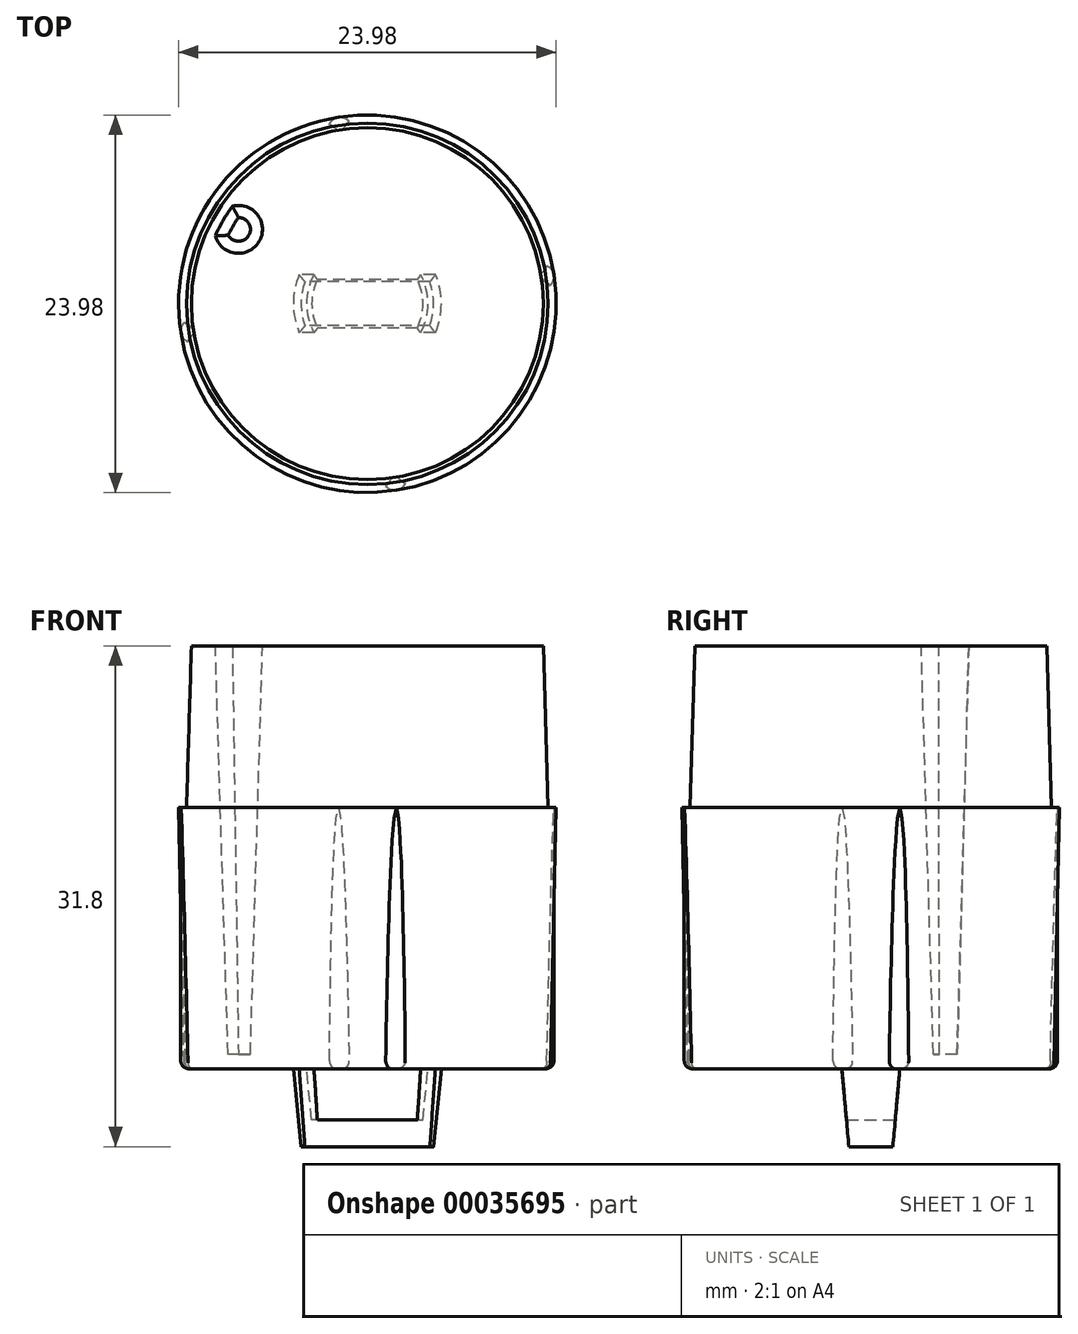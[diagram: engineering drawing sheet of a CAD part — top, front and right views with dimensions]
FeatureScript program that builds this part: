
annotation { "Feature Type Name" : "Feature", "Feature Type Description" : "" }
export const myFeature = defineFeature(function(context is Context, id is Id, definition is map)
    precondition{}
    {
        {
            var Q0;
            Q0=qCreatedBy(makeId("Front.planeOp"),FACE);
            var sketch = newSketch(context, id + "F0", { "sketchPlane" : qUnion([Q0])});
            skPoint(sketch, "E0.visualSharp", {"position": v(11.63, 0) * mm});
            skLineSegment(sketch, "E1", {"start": v(0, 0) * mm, "end": v(11.26, 0) * mm});
            skLineSegment(sketch, "E2", {"start": v(11.64, 0.37) * mm, "end": v(11.99, 16.59) * mm});
            skLineSegment(sketch, "E3", {"start": v(11.32, 16.59) * mm, "end": v(11.18, 26.85) * mm});
            skLineSegment(sketch, "E4", {"start": v(10.58, 26.85) * mm, "end": v(9.86, 0.91) * mm});
            skLineSegment(sketch, "E5", {"start": v(9.86, 0.91) * mm, "end": v(0, 0.91) * mm});
            skLineSegment(sketch, "E6", {"start": v(0, -4.95) * mm, "end": v(4.2, -4.95) * mm});
            skLineSegment(sketch, "E7", {"start": v(4.2, -4.95) * mm, "end": v(4.7, 0) * mm});
            skLineSegment(sketch, "E8", {"start": v(3.53, -3.25) * mm, "end": v(3.95, 0.91) * mm});
            skLineSegment(sketch, "E9", {"start": v(0, -3.25) * mm, "end": v(0, -4.95) * mm});
            skLineSegment(sketch, "E10", {"start": v(11.99, 16.59) * mm, "end": v(11.32, 16.59) * mm});
            skLineSegment(sketch, "E11", {"start": v(11.18, 26.85) * mm, "end": v(10.58, 26.85) * mm});
            skLineSegment(sketch, "E12", {"start": v(0, 0.91) * mm, "end": v(0, 0) * mm});
            skLineSegment(sketch, "E13", {"start": v(0, -3.25) * mm, "end": v(3.53, -3.25) * mm});
            skArc(sketch, "E0.filletArc", {"start": v(11.26, 0) * mm, "mid": v(11.53, 0.1) * mm, "end": v(11.64, 0.37) * mm});
            skSolve(sketch);
        }
        {
            var Q0;
            Q0=makeQuery(id+"F0.imprint","IMPRINT",FACE,{"disambiguationData":[TD([[makeQuery(id+"F0.imprint","IMPRINT",EDGE,{"derivedFrom":sQuery(id+"F0.wireOp",EDGE,"E2")}),1.0]])]});
            var Q1;
            Q1=makeQuery(id+"F0.imprint","IMPRINT",FACE,{"disambiguationData":[TD([[makeQuery(id+"F0.imprint","IMPRINT",EDGE,{"derivedFrom":sQuery(id+"F0.wireOp",EDGE,"E6")}),1.0]])]});
            var Q2;
            Q2=sQuery(id+"F0.wireOp",EDGE,"E12");
            revolve(context, id + "F1", {"entities" : qUnion([Q0, Q1]), "axis" : qUnion([Q2]), "revolveType" : RevolveType.FULL});
        }
        {
            var Q0;
            Q0=qCreatedBy(makeId("Right.planeOp"),FACE);
            var sketch = newSketch(context, id + "F2", { "sketchPlane" : qUnion([Q0])});
            skLineSegment(sketch, "E14", {"start": v(1.84, 0) * mm, "end": v(1.4, -4.95) * mm});
            skLineSegment(sketch, "E15", {"start": v(1.4, -4.95) * mm, "end": v(0, -4.95) * mm});
            skLineSegment(sketch, "E16", {"start": v(1.84, 0) * mm, "end": v(5.88, 0) * mm});
            skLineSegment(sketch, "E17", {"start": v(5.88, 0) * mm, "end": v(5.88, -7.1) * mm});
            skLineSegment(sketch, "E18", {"start": v(5.88, -7.1) * mm, "end": v(0, -7.1) * mm});
            skLineSegment(sketch, "E19.MirrorCS", {"start": v(-1.84, 0) * mm, "end": v(-1.4, -4.95) * mm});
            skLineSegment(sketch, "E20.MirrorCS", {"start": v(-5.88, 0) * mm, "end": v(-5.88, -7.1) * mm});
            skLineSegment(sketch, "E21.MirrorCS", {"start": v(-5.88, -7.1) * mm, "end": v(0, -7.1) * mm});
            skLineSegment(sketch, "E22.MirrorCS", {"start": v(-1.84, 0) * mm, "end": v(-5.88, 0) * mm});
            skLineSegment(sketch, "E23.MirrorCS", {"start": v(-1.4, -4.95) * mm, "end": v(0, -4.95) * mm});
            skLineSegment(sketch, "E24", {"start": v(-1.84, 0) * mm, "end": v(1.84, 0) * mm, "construction": true});
            skPoint(sketch, "E25", {"position": v(0, 0) * mm});
            skLineSegment(sketch, "E26", {"start": v(0, 0) * mm, "end": v(0, -4.95) * mm, "construction": true});
            skCircle(sketch, "E27", {"center": v(0, -4.95) * mm, "radius": 1.4 * mm, "construction": true});
            skCircle(sketch, "E28", {"center": v(0, -7.1) * mm, "radius": 5.88 * mm, "construction": true});
            skCircle(sketch, "E29", {"center": v(0, 0) * mm, "radius": 1.84 * mm, "construction": true});
            skLineSegment(sketch, "E30", {"start": v(0, -4.95) * mm, "end": v(0, -7.1) * mm, "construction": true});
            skSolve(sketch);
        }
        {
            var Q0;
            Q0 = qSketchRegion(id + "F2", true);
            extrude(context, id + "F3", {"entities" : qUnion([Q0]), "operationType" : NewBodyOperationType.REMOVE, "depth" : 25.4 * mm, "symmetric" : true});
        }
        {
            var Q0;
            Q0=makeQuery(id+"F3.boolean.opBoolean","COPY",FACE,{"derivedFrom":makeQuery(id+"F3.opExtrude","SWEPT_FACE",FACE,{"disambiguationData":[OSD([sQuery(id+"F2.wireOp",EDGE,"E19.MirrorCS")])]})});
            var sketch = newSketch(context, id + "F4", { "sketchPlane" : qUnion([Q0])});
            skLineSegment(sketch, "E31", {"start": v(-3.39, 0.16) * mm, "end": v(-3.56, 2.7) * mm});
            skLineSegment(sketch, "E32", {"start": v(-3.56, 2.7) * mm, "end": v(3.56, 2.7) * mm});
            skLineSegment(sketch, "E33", {"start": v(3.56, 2.7) * mm, "end": v(3.39, 0.16) * mm});
            skLineSegment(sketch, "E34", {"start": v(3.39, 0.16) * mm, "end": v(-3.39, 0.16) * mm});
            skLineSegment(sketch, "E35", {"start": v(-3.39, 0.16) * mm, "end": v(-3.17, -3.1) * mm});
            skLineSegment(sketch, "E36", {"start": v(-3.17, -3.1) * mm, "end": v(3.17, -3.1) * mm});
            skLineSegment(sketch, "E37", {"start": v(3.17, -3.1) * mm, "end": v(3.39, 0.16) * mm});
            skSolve(sketch);
        }
        {
            var Q0;
            Q0=makeQuery(id+"F4.imprint","IMPRINT",FACE,{"disambiguationData":[TD([[makeQuery(id+"F4.imprint","IMPRINT",EDGE,{"derivedFrom":sQuery(id+"F4.wireOp",EDGE,"E31")}),-1.0]])]});
            var Q1;
            Q1=makeQuery(id+"F1.opRevolve","SWEPT_FACE",FACE,{"disambiguationData":[OSD([sQuery(id+"F0.wireOp",EDGE,"E8")])]});
            extrude(context, id + "F5", {"entities" : qUnion([Q0]), "operationType" : NewBodyOperationType.ADD, "endBound" : BoundingType.UP_TO_SURFACE, "endBoundEntityFace" : qUnion([Q1]), "depth" : 25.4 * mm});
        }
        {
            var Q0;
            Q0=makeQuery(id+"F3.boolean.opBoolean","COPY",FACE,{"derivedFrom":makeQuery(id+"F3.opExtrude","SWEPT_FACE",FACE,{"disambiguationData":[OSD([sQuery(id+"F2.wireOp",EDGE,"E14")])]})});
            var sketch = newSketch(context, id + "F6", { "sketchPlane" : qUnion([Q0])});
            skLineSegment(sketch, "E38", {"start": v(-3.39, 0.16) * mm, "end": v(-3.17, -3.1) * mm});
            skLineSegment(sketch, "E39", {"start": v(-3.17, -3.1) * mm, "end": v(3.17, -3.1) * mm});
            skLineSegment(sketch, "E40", {"start": v(3.17, -3.1) * mm, "end": v(3.39, 0.16) * mm});
            skLineSegment(sketch, "E41", {"start": v(3.39, 0.16) * mm, "end": v(3.56, 2.7) * mm});
            skLineSegment(sketch, "E42", {"start": v(3.56, 2.7) * mm, "end": v(-3.56, 2.7) * mm});
            skLineSegment(sketch, "E43", {"start": v(-3.56, 2.7) * mm, "end": v(-3.39, 0.16) * mm});
            skLineSegment(sketch, "E44", {"start": v(-3.39, 0.16) * mm, "end": v(3.39, 0.16) * mm});
            skSolve(sketch);
        }
        {
            var Q0;
            Q0=makeQuery(id+"F6.imprint","IMPRINT",FACE,{"disambiguationData":[TD([[makeQuery(id+"F6.imprint","IMPRINT",EDGE,{"derivedFrom":sQuery(id+"F6.wireOp",EDGE,"E41")}),1.0]])]});
            var Q1;
            Q1=makeQuery(id+"F1.opRevolve","SWEPT_FACE",FACE,{"disambiguationData":[OSD([sQuery(id+"F0.wireOp",EDGE,"E8")])]});
            extrude(context, id + "F7", {"entities" : qUnion([Q0]), "operationType" : NewBodyOperationType.ADD, "endBound" : BoundingType.UP_TO_SURFACE, "endBoundEntityFace" : qUnion([Q1]), "depth" : 25.4 * mm});
        }
        {
            var Q0;
            Q0 = qSketchRegion(id + "F2", true);
            extrude(context, id + "F8", {"entities" : qUnion([Q0]), "operationType" : NewBodyOperationType.REMOVE, "oppositeDirection" : true, "depth" : 25.4 * mm, "symmetric" : true});
        }
        {
            var Q0;
            Q0=qCreatedBy(makeId("Front.planeOp"),FACE);
            var sketch = newSketch(context, id + "F9", { "sketchPlane" : qUnion([Q0])});
            skLineSegment(sketch, "E45.0", {"start": v(9.86, 0.91) * mm, "end": v(0, 0.91) * mm});
            skLineSegment(sketch, "E46.1", {"start": v(10.58, 26.85) * mm, "end": v(9.86, 0.91) * mm});
            skLineSegment(sketch, "E47", {"start": v(0, 0.91) * mm, "end": v(0, 26.85) * mm});
            skLineSegment(sketch, "E48", {"start": v(0, 26.85) * mm, "end": v(10.58, 26.85) * mm});
            skSolve(sketch);
        }
        {
            var Q0;
            Q0=makeQuery(id+"F9.imprint","IMPRINT",FACE,{"disambiguationData":[TD([[makeQuery(id+"F9.imprint","IMPRINT",EDGE,{"derivedFrom":sQuery(id+"F9.wireOp",EDGE,"E45.0")}),-1.0]])]});
            var Q1;
            Q1=sQuery(id+"F9.wireOp",EDGE,"E47");
            revolve(context, id + "F10", {"operationType" : NewBodyOperationType.REMOVE, "entities" : qUnion([Q0]), "axis" : qUnion([Q1]), "revolveType" : RevolveType.FULL, "oppositeDirection" : true});
        }
        {
            var Q0;
            Q0=makeQuery(id+"F1.opRevolve","SWEPT_FACE",FACE,{"disambiguationData":[OSD([sQuery(id+"F0.wireOp",EDGE,"E11")])]});
            var sketch = newSketch(context, id + "F11", { "sketchPlane" : qUnion([Q0])});
            skPoint(sketch, "E49", {"position": v(0, -7.92) * mm});
            skCircle(sketch, "E50.MirrorC", {"center": v(8.18, 4.72) * mm, "radius": 1.52 * mm});
            skCircle(sketch, "E51.MirrorC", {"center": v(-8.18, 4.72) * mm, "radius": 1.52 * mm});
            skLineSegment(sketch, "E52", {"start": v(0, 0) * mm, "end": v(9.68, 5.59) * mm, "construction": true});
            skCircle(sketch, "E53", {"center": v(0, -9.45) * mm, "radius": 1.52 * mm});
            skCircle(sketch, "E54.0", {"center": v(0, 0) * mm, "radius": 11.18 * mm, "construction": true});
            skLineSegment(sketch, "E55", {"start": v(0, 0) * mm, "end": v(0, -11.18) * mm, "construction": true});
            skCircle(sketch, "E56.0", {"center": v(0, 0) * mm, "radius": 10.58 * mm, "construction": true});
            skLineSegment(sketch, "E57", {"start": v(1.08, -10.52) * mm, "end": v(1.08, -10.52) * mm});
            skLineSegment(sketch, "E58", {"start": v(0, 0) * mm, "end": v(10.58, 0) * mm, "construction": true});
            skLineSegment(sketch, "E59", {"start": v(10.58, 0) * mm, "end": v(11.18, 0) * mm, "construction": true});
            skSolve(sketch);
        }
        {
            var Q0;
            Q0=makeQuery(id+"F10.boolean.opBoolean","MERGE",FACE,{"derivedFrom":[makeQuery(id+"F1.opRevolve","SWEPT_FACE",FACE,{"disambiguationData":[OSD([sQuery(id+"F0.wireOp",EDGE,"E5")])]}),makeQuery(id+"F10.opRevolve","SWEPT_FACE",FACE,{"disambiguationData":[OSD([sQuery(id+"F9.wireOp",EDGE,"E45.0")])]})]});
            var sketch = newSketch(context, id + "F12", { "sketchPlane" : qUnion([Q0])});
            skCircle(sketch, "E60.0", {"center": v(0, 0) * mm, "radius": 9.86 * mm, "construction": true});
            skLineSegment(sketch, "E61", {"start": v(0, 0) * mm, "end": v(0, -9.86) * mm, "construction": true});
            skLineSegment(sketch, "E62", {"start": v(2.3, -9.58) * mm, "end": v(2.3, -9.58) * mm});
            skCircle(sketch, "E63", {"center": v(0, -9.6) * mm, "radius": 2.3 * mm});
            skPoint(sketch, "E64", {"position": v(0, -7.3) * mm});
            skLineSegment(sketch, "E65", {"start": v(0, 0) * mm, "end": v(9.86, 0) * mm, "construction": true});
            skSolve(sketch);
        }
        {
            var Q0;
            {var subQ0=makeQuery(id+"F1.opRevolve","SWEPT_EDGE",EDGE,{"disambiguationData":[OSD([sQuery(id+"F0.wireOp",EDGE,"E4"),sQuery(id+"F0.wireOp",EDGE,"E11")])]});var subQ1=sQuery(id+"F11.wireOp",EDGE,"E50.MirrorC");var subQ3=makeQuery(id+"F11.imprint","INTERSECT",VERTEX,{"disambiguationData":[OD(0.0)],"derivedFrom":[subQ0,subQ1]});Q0=makeQuery(id+"F11.imprint","IMPRINT",FACE,{"disambiguationData":[TD([[makeQuery(id+"F11.imprint","IMPRINT",EDGE,{"disambiguationData":[TD([[subQ3,-1.0]])],"derivedFrom":subQ1}),1.0]])]});}
            var Q1;
            {var subQ0=makeQuery(id+"F1.opRevolve","SWEPT_EDGE",EDGE,{"disambiguationData":[OSD([sQuery(id+"F0.wireOp",EDGE,"E4"),sQuery(id+"F0.wireOp",EDGE,"E11")])]});var subQ1=sQuery(id+"F11.wireOp",EDGE,"E50.MirrorC");var subQ3=makeQuery(id+"F11.imprint","INTERSECT",VERTEX,{"disambiguationData":[OD(0.0)],"derivedFrom":[subQ0,subQ1]});Q1=makeQuery(id+"F11.imprint","IMPRINT",FACE,{"disambiguationData":[TD([[makeQuery(id+"F11.imprint","IMPRINT",EDGE,{"disambiguationData":[TD([[subQ3,1.0]])],"derivedFrom":subQ1}),1.0]])]});}
            var Q2;
            {var subQ0=makeQuery(id+"F1.opRevolve","SWEPT_EDGE",EDGE,{"disambiguationData":[OSD([sQuery(id+"F0.wireOp",EDGE,"E4"),sQuery(id+"F0.wireOp",EDGE,"E11")])]});var subQ1=sQuery(id+"F11.wireOp",EDGE,"E51.MirrorC");var subQ3=makeQuery(id+"F11.imprint","INTERSECT",VERTEX,{"disambiguationData":[OD(0.0)],"derivedFrom":[subQ0,subQ1]});Q2=makeQuery(id+"F11.imprint","IMPRINT",FACE,{"disambiguationData":[TD([[makeQuery(id+"F11.imprint","IMPRINT",EDGE,{"disambiguationData":[TD([[subQ3,1.0]])],"derivedFrom":subQ1}),-1.0]])]});}
            var Q3;
            {var subQ0=makeQuery(id+"F1.opRevolve","SWEPT_EDGE",EDGE,{"disambiguationData":[OSD([sQuery(id+"F0.wireOp",EDGE,"E4"),sQuery(id+"F0.wireOp",EDGE,"E11")])]});var subQ1=sQuery(id+"F11.wireOp",EDGE,"E51.MirrorC");var subQ3=makeQuery(id+"F11.imprint","INTERSECT",VERTEX,{"disambiguationData":[OD(0.0)],"derivedFrom":[subQ0,subQ1]});Q3=makeQuery(id+"F11.imprint","IMPRINT",FACE,{"disambiguationData":[TD([[makeQuery(id+"F11.imprint","IMPRINT",EDGE,{"disambiguationData":[TD([[subQ3,-1.0]])],"derivedFrom":subQ1}),-1.0]])]});}
            var Q4;
            {var subQ0=makeQuery(id+"F1.opRevolve","SWEPT_EDGE",EDGE,{"disambiguationData":[OSD([sQuery(id+"F0.wireOp",EDGE,"E4"),sQuery(id+"F0.wireOp",EDGE,"E11")])]});var subQ1=sQuery(id+"F11.wireOp",EDGE,"E53");var subQ3=makeQuery(id+"F11.imprint","INTERSECT",VERTEX,{"disambiguationData":[OD(0.0)],"derivedFrom":[subQ0,subQ1]});Q4=makeQuery(id+"F11.imprint","IMPRINT",FACE,{"disambiguationData":[TD([[makeQuery(id+"F11.imprint","IMPRINT",EDGE,{"disambiguationData":[TD([[subQ3,1.0]])],"derivedFrom":subQ1}),1.0]])]});}
            var Q5;
            {var subQ0=makeQuery(id+"F1.opRevolve","SWEPT_EDGE",EDGE,{"disambiguationData":[OSD([sQuery(id+"F0.wireOp",EDGE,"E4"),sQuery(id+"F0.wireOp",EDGE,"E11")])]});var subQ1=sQuery(id+"F11.wireOp",EDGE,"E53");var subQ3=makeQuery(id+"F11.imprint","INTERSECT",VERTEX,{"disambiguationData":[OD(0.0)],"derivedFrom":[subQ0,subQ1]});Q5=makeQuery(id+"F11.imprint","IMPRINT",FACE,{"disambiguationData":[TD([[makeQuery(id+"F11.imprint","IMPRINT",EDGE,{"disambiguationData":[TD([[subQ3,-1.0]])],"derivedFrom":subQ1}),1.0]])]});}
            var Q6;
            Q6=qCreatedBy(makeId("Top.planeOp"),FACE);
            extrude(context, id + "F13", {"entities" : qUnion([Q0, Q1, Q2, Q3, Q4, Q5]), "operationType" : NewBodyOperationType.ADD, "endBound" : BoundingType.UP_TO_SURFACE, "oppositeDirection" : true, "endBoundEntityFace" : qUnion([Q6]), "depth" : 25.4 * mm, "hasDraft" : true, "draftAngle" : 1.7 * degree});
        }
        {
            var Q0;
            Q0=qCreatedBy(makeId("Front.planeOp"),FACE);
            var sketch = newSketch(context, id + "F14", { "sketchPlane" : qUnion([Q0])});
            skLineSegment(sketch, "E66.0", {"start": v(11.64, 0.37) * mm, "end": v(11.99, 16.59) * mm});
            skArc(sketch, "E67.1", {"start": v(11.26, 0) * mm, "mid": v(11.53, 0.1) * mm, "end": v(11.64, 0.37) * mm});
            skLineSegment(sketch, "E68", {"start": v(11.26, 0) * mm, "end": v(4.7, 0) * mm});
            skLineSegment(sketch, "E69", {"start": v(4.7, 0) * mm, "end": v(4.2, -4.95) * mm});
            skLineSegment(sketch, "E70", {"start": v(4.2, -4.95) * mm, "end": v(14.53, -4.95) * mm});
            skLineSegment(sketch, "E71", {"start": v(14.53, -4.95) * mm, "end": v(14.53, 16.59) * mm});
            skLineSegment(sketch, "E72", {"start": v(14.53, 16.59) * mm, "end": v(11.99, 16.59) * mm});
            skLineSegment(sketch, "E73", {"start": v(0, 0) * mm, "end": v(0, 26.85) * mm, "construction": true});
            skSolve(sketch);
        }
        {
            var Q0;
            Q0=makeQuery(id+"F14.imprint","IMPRINT",FACE,{"disambiguationData":[TD([[makeQuery(id+"F14.imprint","IMPRINT",EDGE,{"derivedFrom":sQuery(id+"F14.wireOp",EDGE,"E66.0")}),-1.0]])]});
            var Q1;
            Q1=sQuery(id+"F14.wireOp",EDGE,"E73");
            revolve(context, id + "F15", {"operationType" : NewBodyOperationType.REMOVE, "entities" : qUnion([Q0]), "axis" : qUnion([Q1]), "revolveType" : RevolveType.FULL, "oppositeDirection" : true});
        }
        {
            var Q0;
            Q0=qCreatedBy(makeId("Top.planeOp"),FACE);
            var sketch = newSketch(context, id + "F16", { "sketchPlane" : qUnion([Q0])});
            skCircle(sketch, "E74.0", {"center": v(0, 0) * mm, "radius": 11.99 * mm, "construction": true});
            skLineSegment(sketch, "E75", {"start": v(-4.32, -1.84) * mm, "end": v(-11.85, -1.84) * mm, "construction": true});
            skLineSegment(sketch, "E76", {"start": v(-11.85, -1.84) * mm, "end": v(0, 0) * mm, "construction": true});
            skCircle(sketch, "E77", {"center": v(-11.13, -1.73) * mm, "radius": 0.73 * mm});
            skLineSegment(sketch, "E78", {"start": v(0, 0) * mm, "end": v(11.99, 0) * mm, "construction": true});
            skLineSegment(sketch, "E79", {"start": v(0, 0) * mm, "end": v(0, 11.99) * mm, "construction": true});
            skLineSegment(sketch, "E80", {"start": v(0, 0) * mm, "end": v(1.84, -11.85) * mm, "construction": true});
            skCircle(sketch, "E81.MirrorC", {"center": v(11.13, 1.73) * mm, "radius": 0.73 * mm});
            skLineSegment(sketch, "E82", {"start": v(-11.85, -1.84) * mm, "end": v(1.84, -11.85) * mm, "construction": true});
            skLineSegment(sketch, "E83", {"start": v(0, 0) * mm, "end": v(-5, -6.84) * mm, "construction": true});
            skCircle(sketch, "E84.MirrorC", {"center": v(1.73, -11.13) * mm, "radius": 0.73 * mm});
            skCircle(sketch, "E85.MirrorC", {"center": v(-1.73, 11.13) * mm, "radius": 0.73 * mm});
            skSolve(sketch);
        }
        {
            var Q0;
            Q0 = qSketchRegion(id + "F16", true);
            var Q1;
            Q1=makeQuery(id+"F1.opRevolve","SWEPT_FACE",FACE,{"disambiguationData":[OSD([sQuery(id+"F0.wireOp",EDGE,"E10")])]});
            extrude(context, id + "F17", {"entities" : qUnion([Q0]), "operationType" : NewBodyOperationType.ADD, "endBound" : BoundingType.UP_TO_SURFACE, "endBoundEntityFace" : qUnion([Q1]), "depth" : 25.4 * mm});
        }
        {
            var Q0;
            Q0=makeQuery(id+"F17.opExtrude","CAP_EDGE",EDGE,{"disambiguationData":[OSD([sQuery(id+"F16.wireOp",EDGE,"E84.MirrorC")])],"isStart":true});
            var Q1;
            Q1=makeQuery(id+"F17.opExtrude","CAP_EDGE",EDGE,{"disambiguationData":[OSD([sQuery(id+"F16.wireOp",EDGE,"E81.MirrorC")])],"isStart":true});
            var Q2;
            Q2=makeQuery(id+"F17.opExtrude","CAP_EDGE",EDGE,{"disambiguationData":[OSD([sQuery(id+"F16.wireOp",EDGE,"E85.MirrorC")])],"isStart":true});
            var Q3;
            Q3=makeQuery(id+"F17.opExtrude","CAP_EDGE",EDGE,{"disambiguationData":[OSD([sQuery(id+"F16.wireOp",EDGE,"E77")])],"isStart":true});
            fillet(context, id + "F18", {"entities" : qUnion([Q0, Q1, Q2, Q3]), "radius" : 0.5 * mm, "allowEdgeOverflow" : false});
        }
    });
